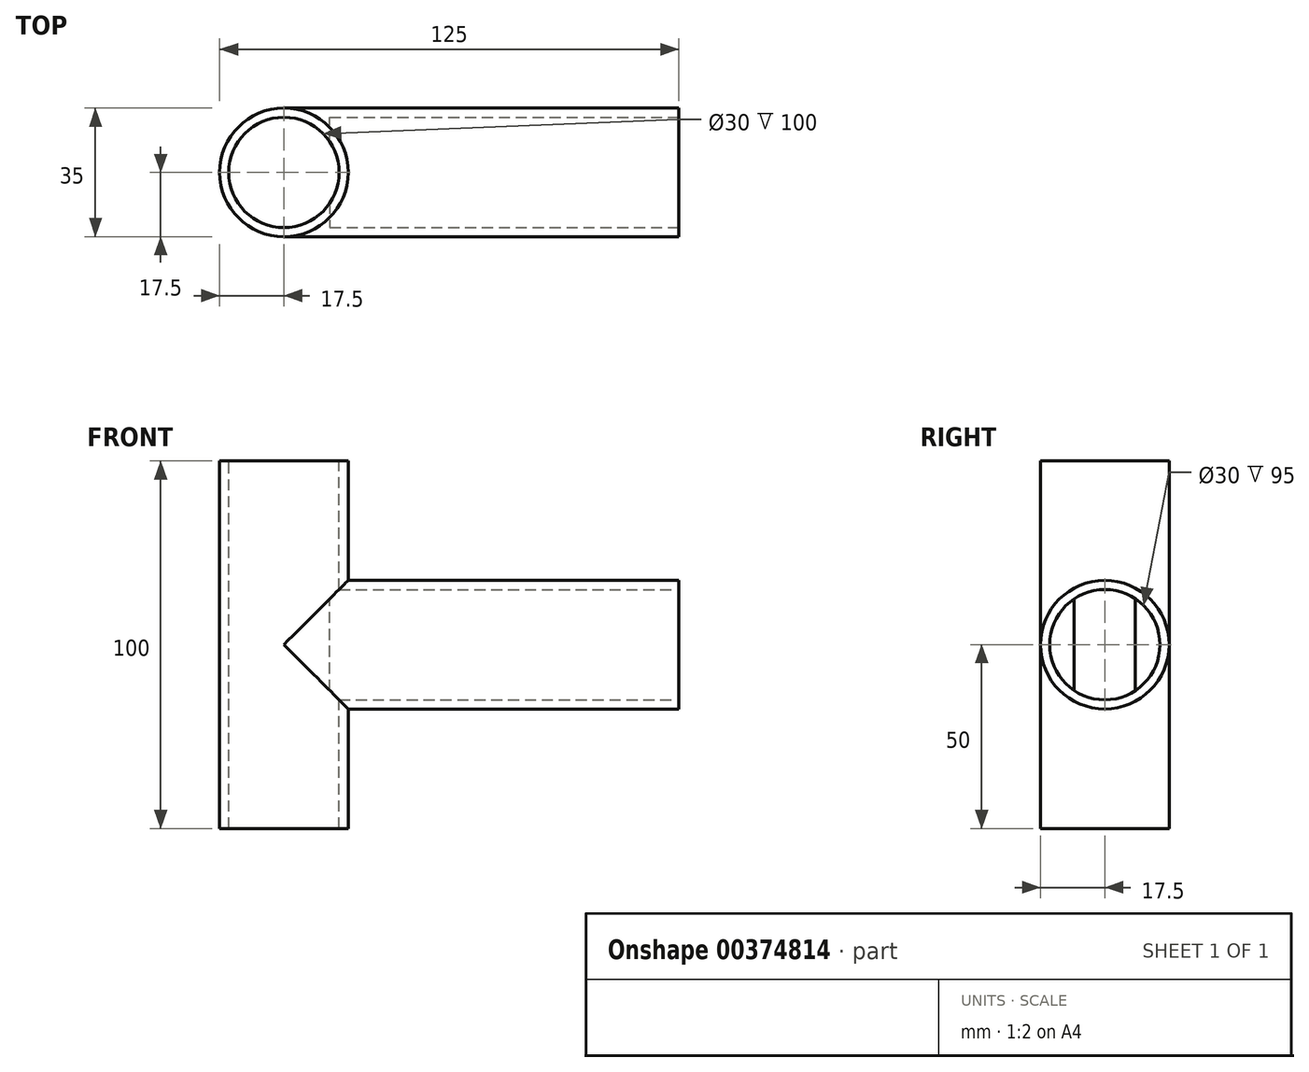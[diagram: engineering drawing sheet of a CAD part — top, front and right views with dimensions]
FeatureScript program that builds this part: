
annotation { "Feature Type Name" : "Feature", "Feature Type Description" : "" }
export const myFeature = defineFeature(function(context is Context, id is Id, definition is map)
    precondition{}
    {
        {
            var Q0;
            Q0=qCreatedBy(makeId("Top.planeOp"),FACE);
            var sketch = newSketch(context, id + "F0", { "sketchPlane" : qUnion([Q0])});
            skCircle(sketch, "E0", {"center": v(0, 0) * mm, "radius": 17.5 * mm});
            skSolve(sketch);
        }
        {
            var Q0;
            Q0 = qSketchRegion(id + "F0", true);
            extrude(context, id + "F1", {"entities" : qUnion([Q0]), "depth" : 100 * mm, "offsetDistance" : 25 * mm});
        }
        {
            var Q0;
            Q0=qCreatedBy(makeId("Right.planeOp"),FACE);
            cPlane(context, id + "F2", {"entities" : qUnion([Q0]), "cplaneType" : CPlaneType.OFFSET, "offset" : 107.5 * mm, "width" : 150 * mm, "height" : 150 * mm});
        }
        {
            var Q0;
            Q0=qCreatedBy(id+"F2.planeOp",FACE);
            var sketch = newSketch(context, id + "F3", { "sketchPlane" : qUnion([Q0])});
            skCircle(sketch, "E1", {"center": v(0, 50) * mm, "radius": 17.5 * mm});
            skSolve(sketch);
        }
        {
            var Q0;
            Q0=makeQuery(id+"F3.imprint","IMPRINT",FACE,{"disambiguationData":[TD([[makeQuery(id+"F3.imprint","IMPRINT",EDGE,{"derivedFrom":sQuery(id+"F3.wireOp",EDGE,"E1")}),1.0]])]});
            extrude(context, id + "F4", {"entities" : qUnion([Q0]), "operationType" : NewBodyOperationType.ADD, "oppositeDirection" : true, "depth" : 107.5 * mm, "offsetDistance" : 25 * mm});
        }
        {
            var Q0;
            Q0=makeQuery(id+"F4.opExtrude","CAP_FACE",FACE,{"disambiguationData":[OSD([sQuery(id+"F3.wireOp",EDGE,"E1")])],"isStart":true});
            var sketch = newSketch(context, id + "F5", { "sketchPlane" : qUnion([Q0])});
            skCircle(sketch, "E2", {"center": v(0, 50) * mm, "radius": 15 * mm});
            skSolve(sketch);
        }
        {
            var Q0;
            Q0=makeQuery(id+"F1.opExtrude","CAP_FACE",FACE,{"disambiguationData":[OSD([sQuery(id+"F0.wireOp",EDGE,"E0")])],"isStart":false});
            var sketch = newSketch(context, id + "F6", { "sketchPlane" : qUnion([Q0])});
            skCircle(sketch, "E3", {"center": v(0, 0) * mm, "radius": 15 * mm});
            skSolve(sketch);
        }
        {
            var Q0;
            Q0=makeQuery(id+"F5.imprint","IMPRINT",FACE,{"disambiguationData":[TD([[makeQuery(id+"F5.imprint","IMPRINT",EDGE,{"derivedFrom":sQuery(id+"F5.wireOp",EDGE,"E2")}),1.0]])]});
            extrude(context, id + "F7", {"entities" : qUnion([Q0]), "operationType" : NewBodyOperationType.REMOVE, "oppositeDirection" : true, "depth" : 95 * mm, "offsetDistance" : 25 * mm});
        }
        {
            var Q0;
            Q0=makeQuery(id+"F6.imprint","IMPRINT",FACE,{"disambiguationData":[TD([[makeQuery(id+"F6.imprint","IMPRINT",EDGE,{"derivedFrom":sQuery(id+"F6.wireOp",EDGE,"E3")}),1.0]])]});
            var Q1;
            Q1=makeQuery(id+"F1.opExtrude","CAP_FACE",FACE,{"disambiguationData":[OSD([sQuery(id+"F0.wireOp",EDGE,"E0")])],"isStart":true});
            extrude(context, id + "F8", {"entities" : qUnion([Q0]), "operationType" : NewBodyOperationType.REMOVE, "endBound" : BoundingType.UP_TO_SURFACE, "oppositeDirection" : true, "depth" : 25 * mm, "endBoundEntityFace" : qUnion([Q1]), "offsetDistance" : 25 * mm});
        }
    });
